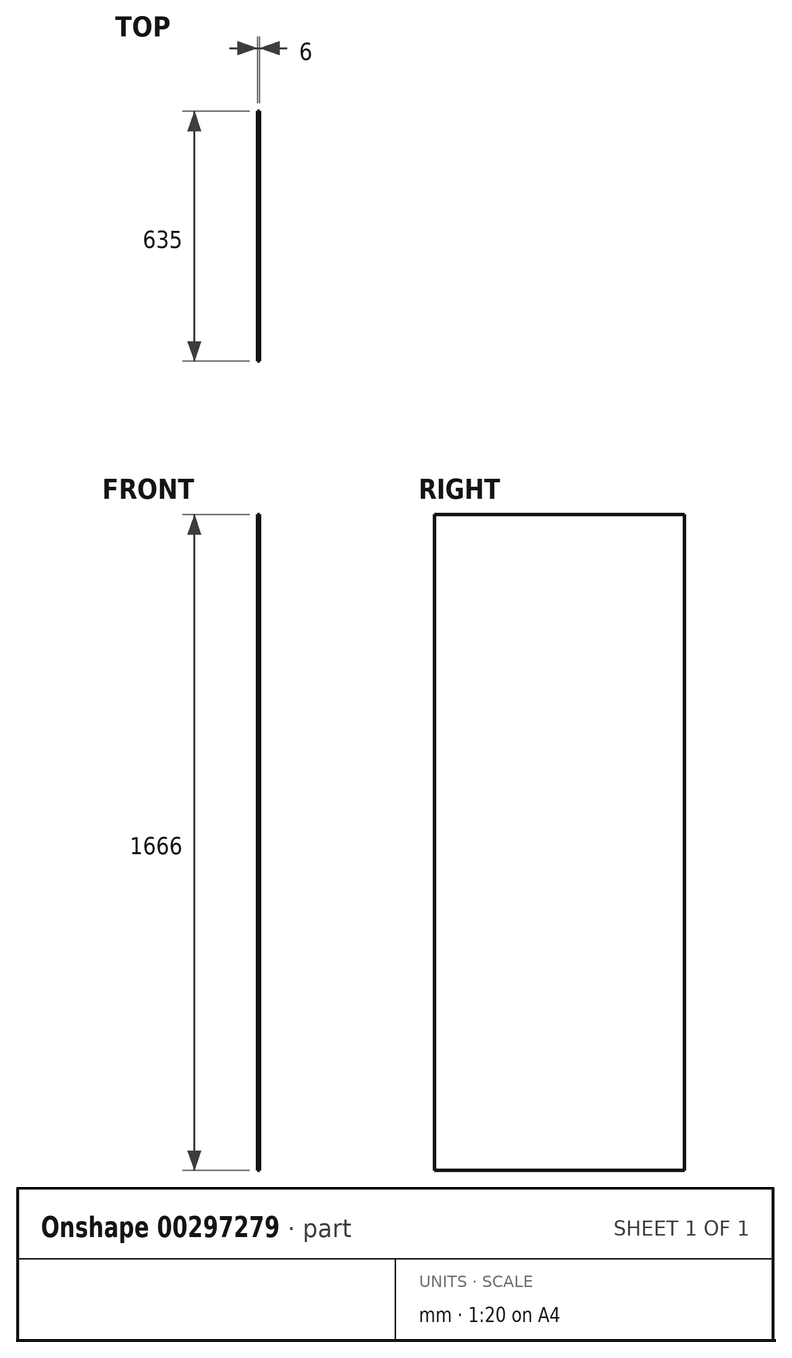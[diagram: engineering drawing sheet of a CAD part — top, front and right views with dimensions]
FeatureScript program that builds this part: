
annotation { "Feature Type Name" : "Feature", "Feature Type Description" : "" }
export const myFeature = defineFeature(function(context is Context, id is Id, definition is map)
    precondition{}
    {
        {
            var Q0;
            Q0=qCreatedBy(makeId("Right.planeOp"),FACE);
            var sketch = newSketch(context, id + "F0", { "sketchPlane" : qUnion([Q0])});
            skLineSegment(sketch, "E0.bottom", {"start": v(317.5, 833) * mm, "end": v(-317.5, 833) * mm});
            skLineSegment(sketch, "E0.top", {"start": v(317.5, -833) * mm, "end": v(-317.5, -833) * mm});
            skLineSegment(sketch, "E0.left", {"start": v(317.5, 833) * mm, "end": v(317.5, -833) * mm});
            skLineSegment(sketch, "E0.right", {"start": v(-317.5, 833) * mm, "end": v(-317.5, -833) * mm});
            skPoint(sketch, "E0.middle", {"position": v(0, 0) * mm});
            skSolve(sketch);
        }
        {
            var Q0;
            Q0 = qSketchRegion(id + "F0", true);
            extrude(context, id + "F1", {"entities" : qUnion([Q0]), "depth" : 6 * mm});
        }
    });
